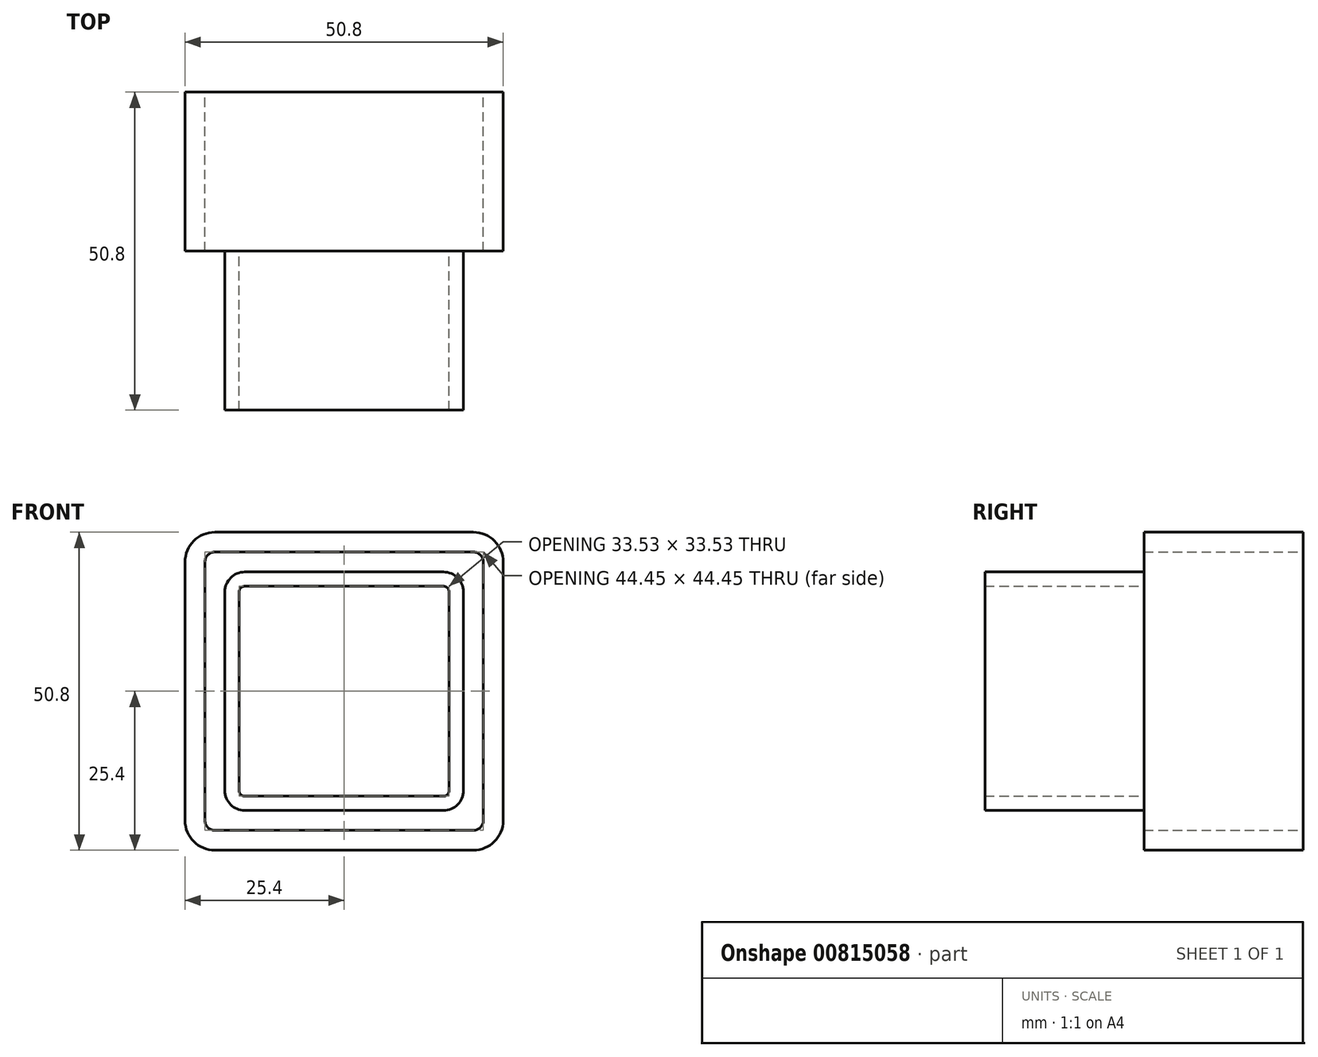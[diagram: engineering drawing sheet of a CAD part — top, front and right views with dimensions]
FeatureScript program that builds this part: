
annotation { "Feature Type Name" : "Feature", "Feature Type Description" : "" }
export const myFeature = defineFeature(function(context is Context, id is Id, definition is map)
    precondition{}
    {
        {
            var Q0;
            Q0=qCreatedBy(makeId("Front.planeOp"),FACE);
            var sketch = newSketch(context, id + "F0", { "sketchPlane" : qUnion([Q0])});
            skLineSegment(sketch, "E0.bottom", {"start": v(25.4, -25.4) * mm, "end": v(-25.4, -25.4) * mm});
            skLineSegment(sketch, "E0.top", {"start": v(25.4, 25.4) * mm, "end": v(-25.4, 25.4) * mm});
            skLineSegment(sketch, "E0.left", {"start": v(25.4, -25.4) * mm, "end": v(25.4, 25.4) * mm});
            skLineSegment(sketch, "E0.right", {"start": v(-25.4, -25.4) * mm, "end": v(-25.4, 25.4) * mm});
            skPoint(sketch, "E0.middle", {"position": v(0, 0) * mm});
            skSolve(sketch);
        }
        {
            var Q0;
            Q0=makeQuery(id+"F0.imprint","IMPRINT",FACE,{"disambiguationData":[TD([[makeQuery(id+"F0.imprint","IMPRINT",EDGE,{"derivedFrom":sQuery(id+"F0.wireOp",EDGE,"E0.bottom")}),-1.0]])]});
            extrude(context, id + "F1", {"entities" : qUnion([Q0]), "oppositeDirection" : true, "depth" : 25.4 * mm, "offsetDistance" : 25.4 * mm});
        }
        {
            var Q0;
            Q0=makeQuery(id+"F1.opExtrude","SWEPT_EDGE",EDGE,{"disambiguationData":[OSD([sQuery(id+"F0.wireOp",EDGE,"E0.top"),sQuery(id+"F0.wireOp",EDGE,"E0.right")])]});
            var Q1;
            Q1=makeQuery(id+"F1.opExtrude","SWEPT_EDGE",EDGE,{"disambiguationData":[OSD([sQuery(id+"F0.wireOp",EDGE,"E0.top"),sQuery(id+"F0.wireOp",EDGE,"E0.left")])]});
            var Q2;
            Q2=makeQuery(id+"F1.opExtrude","SWEPT_EDGE",EDGE,{"disambiguationData":[OSD([sQuery(id+"F0.wireOp",EDGE,"E0.bottom"),sQuery(id+"F0.wireOp",EDGE,"E0.left")])]});
            var Q3;
            Q3=makeQuery(id+"F1.opExtrude","SWEPT_EDGE",EDGE,{"disambiguationData":[OSD([sQuery(id+"F0.wireOp",EDGE,"E0.bottom"),sQuery(id+"F0.wireOp",EDGE,"E0.right")])]});
            fillet(context, id + "F2", {"entities" : qUnion([Q0, Q1, Q2, Q3]), "radius" : 4.75 * mm, "tangentPropagation" : true, "allowEdgeOverflow" : false});
        }
        {
            var Q0;
            Q0=makeQuery(id+"F1.opExtrude","CAP_FACE",FACE,{"disambiguationData":[OSD([sQuery(id+"F0.wireOp",EDGE,"E0.bottom"),sQuery(id+"F0.wireOp",EDGE,"E0.top"),sQuery(id+"F0.wireOp",EDGE,"E0.left"),sQuery(id+"F0.wireOp",EDGE,"E0.right")])],"isStart":false});
            var Q1;
            Q1=makeQuery(id+"F1.opExtrude","CAP_FACE",FACE,{"disambiguationData":[OSD([sQuery(id+"F0.wireOp",EDGE,"E0.bottom"),sQuery(id+"F0.wireOp",EDGE,"E0.top"),sQuery(id+"F0.wireOp",EDGE,"E0.left"),sQuery(id+"F0.wireOp",EDGE,"E0.right")])],"isStart":true});
            shell(context, id + "F3", {"entities" : qUnion([Q0, Q1]), "thickness" : 3.17 * mm});
        }
        {
            var Q0;
            Q0=qCreatedBy(makeId("Front.planeOp"),FACE);
            var sketch = newSketch(context, id + "F4", { "sketchPlane" : qUnion([Q0])});
            skLineSegment(sketch, "E1.bottom", {"start": v(19.05, -19.05) * mm, "end": v(-19.05, -19.05) * mm});
            skLineSegment(sketch, "E1.top", {"start": v(19.05, 19.05) * mm, "end": v(-19.05, 19.05) * mm});
            skLineSegment(sketch, "E1.left", {"start": v(19.05, -19.05) * mm, "end": v(19.05, 19.05) * mm});
            skLineSegment(sketch, "E1.right", {"start": v(-19.05, -19.05) * mm, "end": v(-19.05, 19.05) * mm});
            skPoint(sketch, "E1.middle", {"position": v(0, 0) * mm});
            skSolve(sketch);
        }
        {
            var Q0;
            Q0=makeQuery(id+"F4.imprint","IMPRINT",FACE,{"disambiguationData":[TD([[makeQuery(id+"F4.imprint","IMPRINT",EDGE,{"derivedFrom":sQuery(id+"F4.wireOp",EDGE,"E1.bottom")}),-1.0]])]});
            extrude(context, id + "F5", {"entities" : qUnion([Q0]), "depth" : 25.4 * mm, "offsetDistance" : 25.4 * mm});
        }
        {
            var Q0;
            Q0=makeQuery(id+"F5.opExtrude","SWEPT_EDGE",EDGE,{"disambiguationData":[OSD([sQuery(id+"F4.wireOp",EDGE,"E1.top"),sQuery(id+"F4.wireOp",EDGE,"E1.right")])]});
            var Q1;
            Q1=makeQuery(id+"F5.opExtrude","SWEPT_EDGE",EDGE,{"disambiguationData":[OSD([sQuery(id+"F4.wireOp",EDGE,"E1.top"),sQuery(id+"F4.wireOp",EDGE,"E1.left")])]});
            var Q2;
            Q2=makeQuery(id+"F5.opExtrude","SWEPT_EDGE",EDGE,{"disambiguationData":[OSD([sQuery(id+"F4.wireOp",EDGE,"E1.bottom"),sQuery(id+"F4.wireOp",EDGE,"E1.left")])]});
            var Q3;
            Q3=makeQuery(id+"F5.opExtrude","SWEPT_EDGE",EDGE,{"disambiguationData":[OSD([sQuery(id+"F4.wireOp",EDGE,"E1.bottom"),sQuery(id+"F4.wireOp",EDGE,"E1.right")])]});
            fillet(context, id + "F6", {"entities" : qUnion([Q0, Q1, Q2, Q3]), "radius" : 3.17 * mm, "tangentPropagation" : true, "allowEdgeOverflow" : false});
        }
        {
            var Q0;
            Q0=makeQuery(id+"F5.opExtrude","CAP_FACE",FACE,{"disambiguationData":[OSD([sQuery(id+"F4.wireOp",EDGE,"E1.bottom"),sQuery(id+"F4.wireOp",EDGE,"E1.top"),sQuery(id+"F4.wireOp",EDGE,"E1.left"),sQuery(id+"F4.wireOp",EDGE,"E1.right")])],"isStart":false});
            var Q1;
            Q1=makeQuery(id+"F5.opExtrude","CAP_FACE",FACE,{"disambiguationData":[OSD([sQuery(id+"F4.wireOp",EDGE,"E1.bottom"),sQuery(id+"F4.wireOp",EDGE,"E1.top"),sQuery(id+"F4.wireOp",EDGE,"E1.left"),sQuery(id+"F4.wireOp",EDGE,"E1.right")])],"isStart":true});
            shell(context, id + "F7", {"entities" : qUnion([Q0, Q1]), "thickness" : 2.3 * mm});
        }
    });
